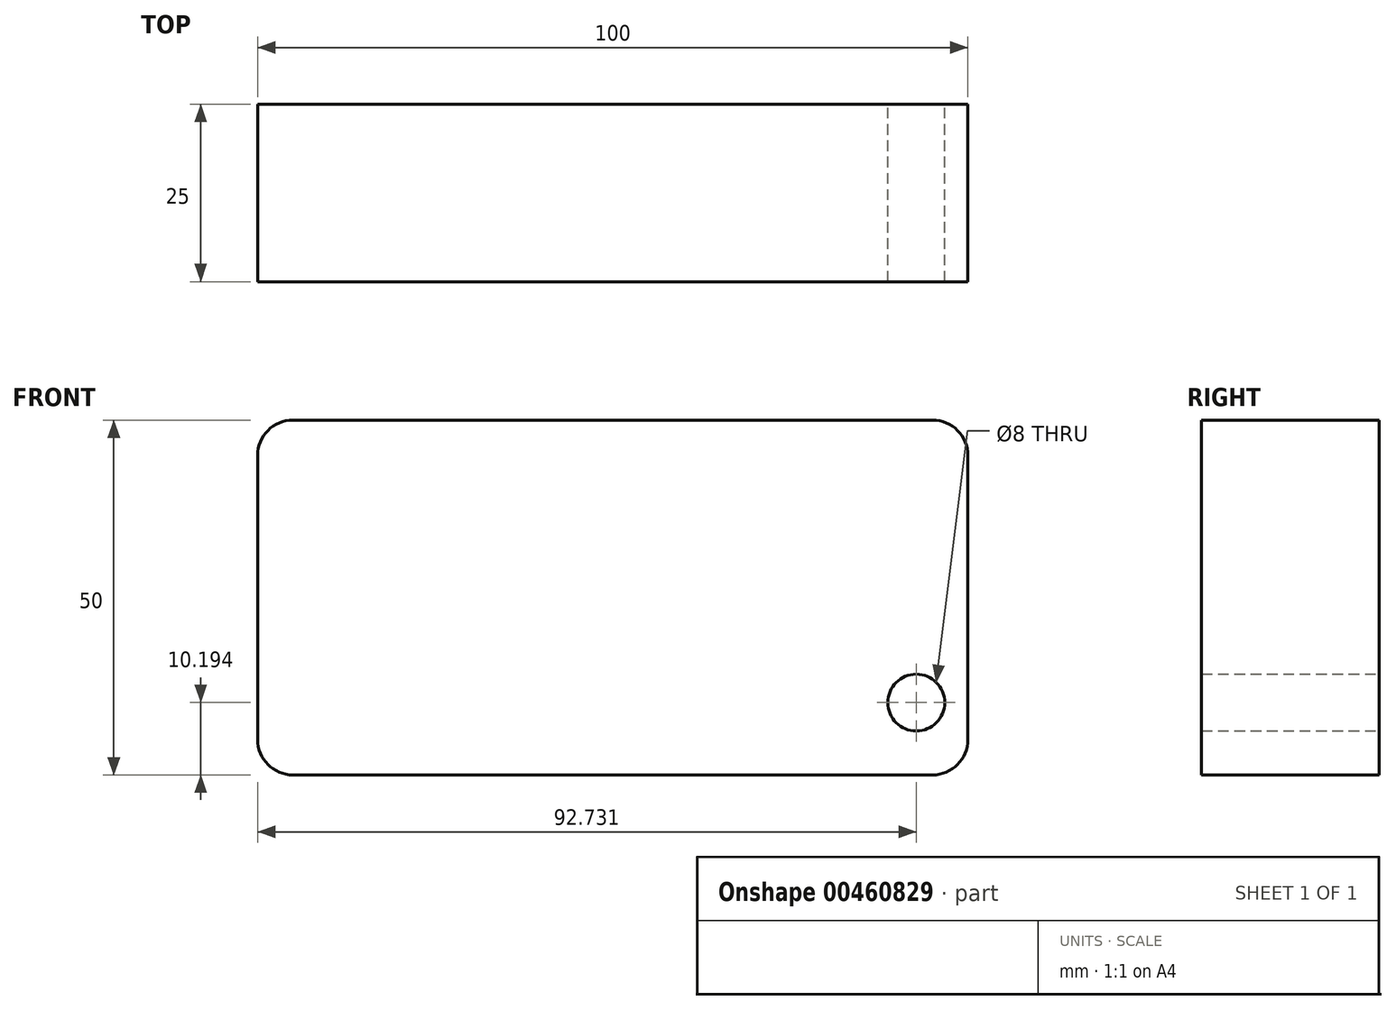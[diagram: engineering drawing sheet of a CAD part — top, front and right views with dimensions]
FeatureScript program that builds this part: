
annotation { "Feature Type Name" : "Feature", "Feature Type Description" : "" }
export const myFeature = defineFeature(function(context is Context, id is Id, definition is map)
    precondition{}
    {
        {
            var Q0;
            Q0=qCreatedBy(makeId("Front.planeOp"),FACE);
            var sketch = newSketch(context, id + "F0", { "sketchPlane" : qUnion([Q0])});
            skLineSegment(sketch, "E0.bottom", {"start": v(-38.42, 16.56) * mm, "end": v(51.58, 16.56) * mm});
            skLineSegment(sketch, "E0.top", {"start": v(-38.42, -33.44) * mm, "end": v(51.58, -33.44) * mm});
            skLineSegment(sketch, "E0.left", {"start": v(-43.42, 11.56) * mm, "end": v(-43.42, -28.44) * mm});
            skLineSegment(sketch, "E0.right", {"start": v(56.58, 11.56) * mm, "end": v(56.58, -28.44) * mm});
            skPoint(sketch, "E1.visualSharp", {"position": v(56.58, 16.56) * mm});
            skArc(sketch, "E1.filletArc", {"start": v(56.58, 11.56) * mm, "mid": v(55.12, 15.1) * mm, "end": v(51.58, 16.56) * mm});
            skPoint(sketch, "E2.visualSharp", {"position": v(56.58, -33.44) * mm});
            skArc(sketch, "E2.filletArc", {"start": v(51.58, -33.44) * mm, "mid": v(55.12, -31.97) * mm, "end": v(56.58, -28.44) * mm});
            skPoint(sketch, "E3.visualSharp", {"position": v(-43.42, 16.56) * mm});
            skArc(sketch, "E3.filletArc", {"start": v(-38.42, 16.56) * mm, "mid": v(-41.95, 15.1) * mm, "end": v(-43.42, 11.56) * mm});
            skPoint(sketch, "E4.visualSharp", {"position": v(-43.42, -33.44) * mm});
            skArc(sketch, "E4.filletArc", {"start": v(-43.42, -28.44) * mm, "mid": v(-41.95, -31.97) * mm, "end": v(-38.42, -33.44) * mm});
            skCircle(sketch, "E5", {"center": v(49.31, -23.25) * mm, "radius": 4 * mm});
            skSolve(sketch);
        }
        {
            var Q0;
            Q0 = qSketchRegion(id + "F0", true);
            extrude(context, id + "F1", {"entities" : qUnion([Q0]), "depth" : 25 * mm});
        }
    });
